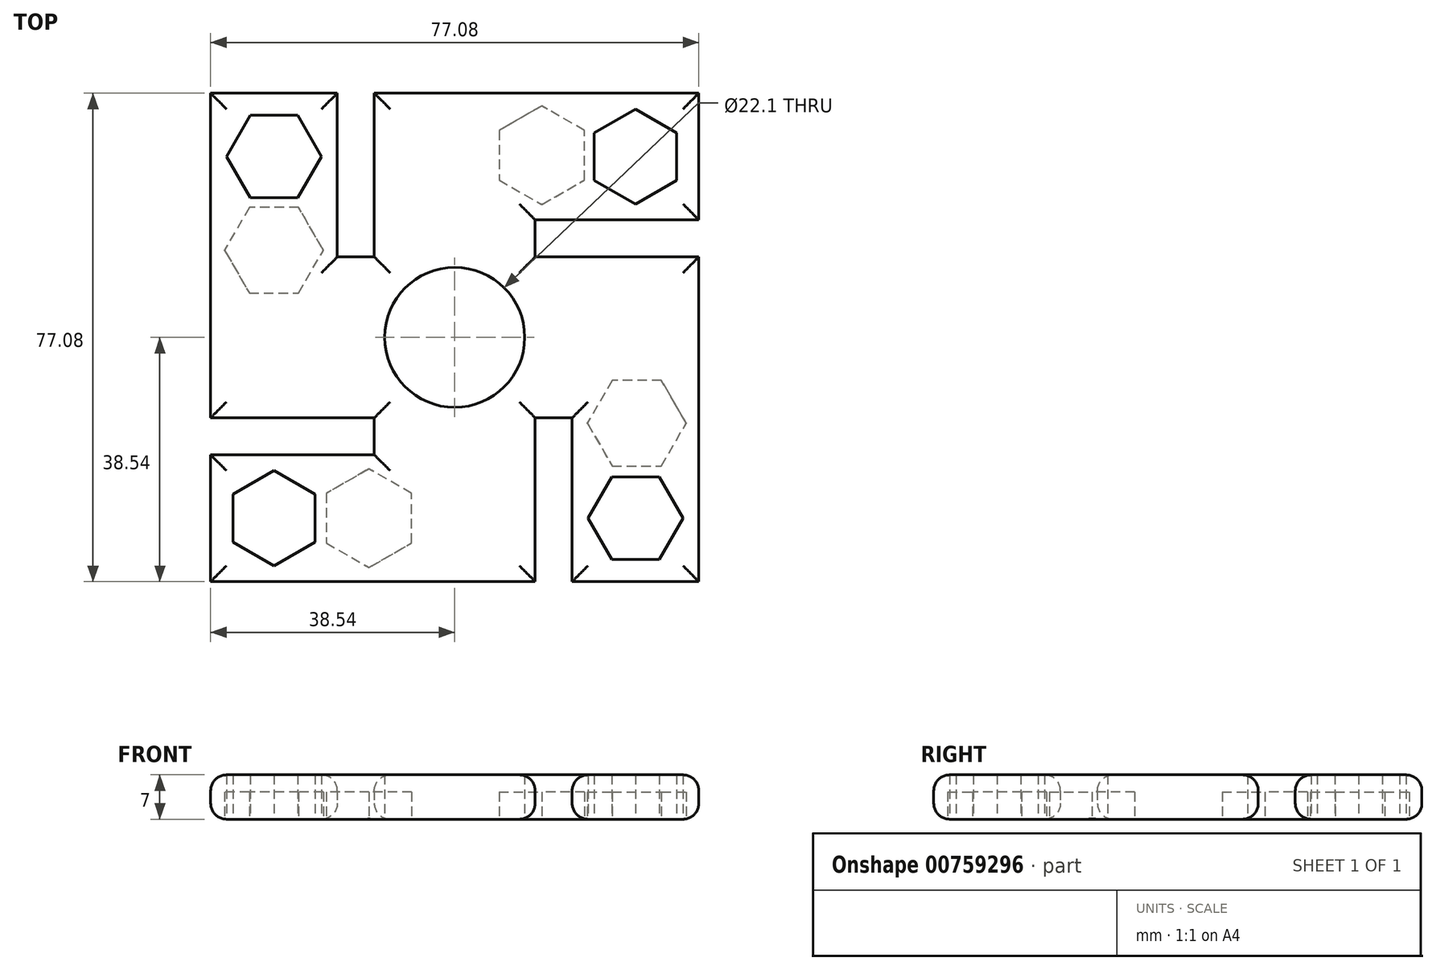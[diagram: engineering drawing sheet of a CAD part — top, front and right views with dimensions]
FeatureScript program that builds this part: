
annotation { "Feature Type Name" : "Feature", "Feature Type Description" : "" }
export const myFeature = defineFeature(function(context is Context, id is Id, definition is map)
    precondition{}
    {
        {
            var Q0;
            Q0=qCreatedBy(makeId("Top.planeOp"),FACE);
            var sketch = newSketch(context, id + "F0", { "sketchPlane" : qUnion([Q0])});
            skCircle(sketch, "E0", {"center": v(0, 0) * mm, "radius": 11.05 * mm});
            skCircle(sketch, "E1", {"center": v(0, 0) * mm, "radius": 12.7 * mm});
            skLineSegment(sketch, "E2.bottom", {"start": v(12.7, 12.7) * mm, "end": v(-12.7, 12.7) * mm});
            skLineSegment(sketch, "E2.top", {"start": v(12.7, -12.7) * mm, "end": v(-12.7, -12.7) * mm});
            skLineSegment(sketch, "E2.left", {"start": v(12.7, 12.7) * mm, "end": v(12.7, -12.7) * mm});
            skLineSegment(sketch, "E2.right", {"start": v(-12.7, 12.7) * mm, "end": v(-12.7, -12.7) * mm});
            skLineSegment(sketch, "E3.bottom", {"start": v(-12.7, 12.7) * mm, "end": v(12.7, 12.7) * mm});
            skLineSegment(sketch, "E3.top", {"start": v(-12.7, 38.54) * mm, "end": v(12.7, 38.54) * mm});
            skLineSegment(sketch, "E3.left", {"start": v(-12.7, 12.7) * mm, "end": v(-12.7, 38.54) * mm});
            skLineSegment(sketch, "E3.right", {"start": v(12.7, 12.7) * mm, "end": v(12.7, 38.54) * mm});
            skLineSegment(sketch, "E4.bottom", {"start": v(12.7, 38.54) * mm, "end": v(38.54, 38.54) * mm});
            skLineSegment(sketch, "E4.top", {"start": v(12.7, 18.54) * mm, "end": v(38.54, 18.54) * mm});
            skLineSegment(sketch, "E4.left", {"start": v(12.7, 38.54) * mm, "end": v(12.7, 18.54) * mm});
            skLineSegment(sketch, "E4.right", {"start": v(38.54, 38.54) * mm, "end": v(38.54, 18.54) * mm});
            skCircle(sketch, "E5.cCircle", {"center": v(28.54, 28.54) * mm, "radius": 6.5 * mm, "construction": true});
            skLineSegment(sketch, "E5.0", {"start": v(35.04, 32.3) * mm, "end": v(35.04, 24.79) * mm});
            skLineSegment(sketch, "E5.1", {"start": v(35.04, 24.79) * mm, "end": v(28.54, 21.03) * mm});
            skLineSegment(sketch, "E5.2", {"start": v(28.54, 21.03) * mm, "end": v(22.04, 24.79) * mm});
            skLineSegment(sketch, "E5.3", {"start": v(22.04, 24.79) * mm, "end": v(22.04, 32.3) * mm});
            skLineSegment(sketch, "E5.4", {"start": v(22.04, 32.3) * mm, "end": v(28.54, 36.05) * mm});
            skLineSegment(sketch, "E5.5", {"start": v(28.54, 36.05) * mm, "end": v(35.04, 32.3) * mm});
            skPoint(sketch, "E5.0.midPoint", {"position": v(35.04, 28.54) * mm});
            skPoint(sketch, "E6.1.0", {"position": v(-28.54, 35.04) * mm});
            skLineSegment(sketch, "E6.1.1", {"start": v(-18.54, 12.7) * mm, "end": v(-18.54, 38.54) * mm});
            skLineSegment(sketch, "E6.1.2", {"start": v(-12.7, -12.7) * mm, "end": v(-38.54, -12.7) * mm});
            skLineSegment(sketch, "E6.1.3", {"start": v(-38.54, 12.7) * mm, "end": v(-38.54, 38.54) * mm});
            skLineSegment(sketch, "E6.1.4", {"start": v(-38.54, -12.7) * mm, "end": v(-38.54, 12.7) * mm});
            skCircle(sketch, "E6.1.5", {"center": v(-28.54, 28.54) * mm, "radius": 6.5 * mm, "construction": true});
            skLineSegment(sketch, "E6.1.6", {"start": v(-12.7, 12.7) * mm, "end": v(-38.54, 12.7) * mm});
            skLineSegment(sketch, "E6.1.7", {"start": v(-12.7, -12.7) * mm, "end": v(-12.7, 12.7) * mm});
            skLineSegment(sketch, "E6.1.8", {"start": v(-38.54, 12.7) * mm, "end": v(-18.54, 12.7) * mm});
            skLineSegment(sketch, "E6.1.9", {"start": v(-38.54, 38.54) * mm, "end": v(-18.54, 38.54) * mm});
            skLineSegment(sketch, "E6.1.10", {"start": v(-32.3, 22.04) * mm, "end": v(-36.05, 28.54) * mm});
            skLineSegment(sketch, "E6.1.11", {"start": v(-21.03, 28.54) * mm, "end": v(-24.79, 22.04) * mm});
            skLineSegment(sketch, "E6.1.12", {"start": v(-24.79, 35.04) * mm, "end": v(-21.03, 28.54) * mm});
            skLineSegment(sketch, "E6.1.13", {"start": v(-36.05, 28.54) * mm, "end": v(-32.3, 35.04) * mm});
            skLineSegment(sketch, "E6.1.15", {"start": v(-24.79, 22.04) * mm, "end": v(-32.3, 22.04) * mm});
            skLineSegment(sketch, "E6.1.16", {"start": v(-32.3, 35.04) * mm, "end": v(-24.79, 35.04) * mm});
            skPoint(sketch, "E6.2.0", {"position": v(-35.04, -28.54) * mm});
            skLineSegment(sketch, "E6.2.1", {"start": v(-12.7, -18.54) * mm, "end": v(-38.54, -18.54) * mm});
            skLineSegment(sketch, "E6.2.2", {"start": v(12.7, -12.7) * mm, "end": v(12.7, -38.54) * mm});
            skLineSegment(sketch, "E6.2.3", {"start": v(-12.7, -38.54) * mm, "end": v(-38.54, -38.54) * mm});
            skLineSegment(sketch, "E6.2.4", {"start": v(12.7, -38.54) * mm, "end": v(-12.7, -38.54) * mm});
            skCircle(sketch, "E6.2.5", {"center": v(-28.54, -28.54) * mm, "radius": 6.5 * mm, "construction": true});
            skLineSegment(sketch, "E6.2.6", {"start": v(-12.7, -12.7) * mm, "end": v(-12.7, -38.54) * mm});
            skLineSegment(sketch, "E6.2.8", {"start": v(-12.7, -38.54) * mm, "end": v(-12.7, -18.54) * mm});
            skLineSegment(sketch, "E6.2.9", {"start": v(-38.54, -38.54) * mm, "end": v(-38.54, -18.54) * mm});
            skLineSegment(sketch, "E6.2.10", {"start": v(-22.04, -32.3) * mm, "end": v(-28.54, -36.05) * mm});
            skLineSegment(sketch, "E6.2.11", {"start": v(-28.54, -21.03) * mm, "end": v(-22.04, -24.79) * mm});
            skLineSegment(sketch, "E6.2.12", {"start": v(-35.04, -24.79) * mm, "end": v(-28.54, -21.03) * mm});
            skLineSegment(sketch, "E6.2.13", {"start": v(-28.54, -36.05) * mm, "end": v(-35.04, -32.3) * mm});
            skLineSegment(sketch, "E6.2.14", {"start": v(-12.7, -12.7) * mm, "end": v(12.7, -12.7) * mm});
            skLineSegment(sketch, "E6.2.15", {"start": v(-22.04, -24.79) * mm, "end": v(-22.04, -32.3) * mm});
            skLineSegment(sketch, "E6.2.16", {"start": v(-35.04, -32.3) * mm, "end": v(-35.04, -24.79) * mm});
            skPoint(sketch, "E6.3.0", {"position": v(28.54, -35.04) * mm});
            skLineSegment(sketch, "E6.3.1", {"start": v(18.54, -12.7) * mm, "end": v(18.54, -38.54) * mm});
            skLineSegment(sketch, "E6.3.2", {"start": v(12.7, 12.7) * mm, "end": v(38.54, 12.7) * mm});
            skLineSegment(sketch, "E6.3.3", {"start": v(38.54, -12.7) * mm, "end": v(38.54, -38.54) * mm});
            skLineSegment(sketch, "E6.3.4", {"start": v(38.54, 12.7) * mm, "end": v(38.54, -12.7) * mm});
            skCircle(sketch, "E6.3.5", {"center": v(28.54, -28.54) * mm, "radius": 6.5 * mm, "construction": true});
            skLineSegment(sketch, "E6.3.6", {"start": v(12.7, -12.7) * mm, "end": v(38.54, -12.7) * mm});
            skLineSegment(sketch, "E6.3.8", {"start": v(38.54, -12.7) * mm, "end": v(18.54, -12.7) * mm});
            skLineSegment(sketch, "E6.3.9", {"start": v(38.54, -38.54) * mm, "end": v(18.54, -38.54) * mm});
            skLineSegment(sketch, "E6.3.10", {"start": v(32.3, -22.04) * mm, "end": v(36.05, -28.54) * mm});
            skLineSegment(sketch, "E6.3.11", {"start": v(21.03, -28.54) * mm, "end": v(24.79, -22.04) * mm});
            skLineSegment(sketch, "E6.3.12", {"start": v(24.79, -35.04) * mm, "end": v(21.03, -28.54) * mm});
            skLineSegment(sketch, "E6.3.13", {"start": v(36.05, -28.54) * mm, "end": v(32.3, -35.04) * mm});
            skLineSegment(sketch, "E6.3.14", {"start": v(12.7, -12.7) * mm, "end": v(12.7, 12.7) * mm});
            skLineSegment(sketch, "E6.3.15", {"start": v(24.79, -22.04) * mm, "end": v(32.3, -22.04) * mm});
            skLineSegment(sketch, "E6.3.16", {"start": v(32.3, -35.04) * mm, "end": v(24.79, -35.04) * mm});
            skSolve(sketch);
        }
        {
            var Q0;
            Q0=makeQuery(id+"F0.imprint","IMPRINT",FACE,{"disambiguationData":[TD([[makeQuery(id+"F0.imprint","IMPRINT",EDGE,{"derivedFrom":sQuery(id+"F0.wireOp",EDGE,"E6.1.1")}),1.0]])]});
            var Q1;
            {var subQ1=sQuery(id+"F0.wireOp",EDGE,"E6.1.2");Q1=makeQuery(id+"F0.imprint","IMPRINT",FACE,{"disambiguationData":[TD([[makeQuery(id+"F0.imprint","IMPRINT",EDGE,{"derivedFrom":subQ1}),-1.0]])]});}
            var Q2;
            {var subQ0=sQuery(id+"F0.wireOp",EDGE,"E3.bottom");var subQ1=sQuery(id+"F0.wireOp",EDGE,"E1");var subQ2=makeQuery(id+"F0.imprint","INTERSECT",VERTEX,{"derivedFrom":[subQ1,subQ0]});Q2=makeQuery(id+"F0.imprint","IMPRINT",FACE,{"disambiguationData":[TD([[makeQuery(id+"F0.imprint","IMPRINT",EDGE,{"disambiguationData":[TD([[subQ2,-1.0]])],"derivedFrom":subQ1}),-1.0]])]});}
            var Q3;
            {var subQ0=sQuery(id+"F0.wireOp",EDGE,"E2.right");var subQ1=sQuery(id+"F0.wireOp",EDGE,"E1");var subQ2=makeQuery(id+"F0.imprint","INTERSECT",VERTEX,{"derivedFrom":[subQ1,subQ0]});Q3=makeQuery(id+"F0.imprint","IMPRINT",FACE,{"disambiguationData":[TD([[makeQuery(id+"F0.imprint","IMPRINT",EDGE,{"disambiguationData":[TD([[subQ2,-1.0]])],"derivedFrom":subQ1}),-1.0]])]});}
            var Q4;
            {var subQ0=sQuery(id+"F0.wireOp",EDGE,"E6.3.14");var subQ1=sQuery(id+"F0.wireOp",EDGE,"E1");var subQ2=makeQuery(id+"F0.imprint","INTERSECT",VERTEX,{"derivedFrom":[subQ1,subQ0]});Q4=makeQuery(id+"F0.imprint","IMPRINT",FACE,{"disambiguationData":[TD([[makeQuery(id+"F0.imprint","IMPRINT",EDGE,{"disambiguationData":[TD([[subQ2,1.0]])],"derivedFrom":subQ1}),-1.0]])]});}
            var Q5;
            {var subQ0=sQuery(id+"F0.wireOp",EDGE,"E3.bottom");var subQ1=sQuery(id+"F0.wireOp",EDGE,"E1");var subQ2=makeQuery(id+"F0.imprint","INTERSECT",VERTEX,{"derivedFrom":[subQ1,subQ0]});Q5=makeQuery(id+"F0.imprint","IMPRINT",FACE,{"disambiguationData":[TD([[makeQuery(id+"F0.imprint","IMPRINT",EDGE,{"disambiguationData":[TD([[subQ2,1.0]])],"derivedFrom":subQ1}),-1.0]])]});}
            var Q6;
            Q6=makeQuery(id+"F0.imprint","IMPRINT",FACE,{"disambiguationData":[TD([[makeQuery(id+"F0.imprint","IMPRINT",EDGE,{"derivedFrom":sQuery(id+"F0.wireOp",EDGE,"E4.bottom")}),-1.0]])]});
            var Q7;
            Q7=makeQuery(id+"F0.imprint","IMPRINT",FACE,{"disambiguationData":[TD([[makeQuery(id+"F0.imprint","IMPRINT",EDGE,{"derivedFrom":sQuery(id+"F0.wireOp",EDGE,"E6.3.1")}),1.0]])]});
            var Q8;
            {var subQ1=sQuery(id+"F0.wireOp",EDGE,"E6.3.2");Q8=makeQuery(id+"F0.imprint","IMPRINT",FACE,{"disambiguationData":[TD([[makeQuery(id+"F0.imprint","IMPRINT",EDGE,{"derivedFrom":subQ1}),-1.0]])]});}
            var Q9;
            {var subQ1=sQuery(id+"F0.wireOp",EDGE,"E6.2.2");Q9=makeQuery(id+"F0.imprint","IMPRINT",FACE,{"disambiguationData":[TD([[makeQuery(id+"F0.imprint","IMPRINT",EDGE,{"derivedFrom":subQ1}),-1.0]])]});}
            var Q10;
            Q10=makeQuery(id+"F0.imprint","IMPRINT",FACE,{"disambiguationData":[TD([[makeQuery(id+"F0.imprint","IMPRINT",EDGE,{"derivedFrom":sQuery(id+"F0.wireOp",EDGE,"E6.2.1")}),1.0]])]});
            var Q11;
            Q11=makeQuery(id+"F0.imprint","IMPRINT",FACE,{"disambiguationData":[TD([[makeQuery(id+"F0.imprint","IMPRINT",EDGE,{"derivedFrom":sQuery(id+"F0.wireOp",EDGE,"E0")}),-1.0]])]});
            var Q12;
            Q12=makeQuery(id+"F0.imprint","IMPRINT",FACE,{"disambiguationData":[TD([[makeQuery(id+"F0.imprint","IMPRINT",EDGE,{"derivedFrom":sQuery(id+"F0.wireOp",EDGE,"E3.top")}),-1.0]])]});
            extrude(context, id + "F1", {"entities" : qUnion([Q0, Q1, Q2, Q3, Q4, Q5, Q6, Q7, Q8, Q9, Q10, Q11, Q12]), "depth" : 7 * mm, "offsetDistance" : 25 * mm});
        }
        {
            var Q0;
            Q0=makeQuery(id+"F1.opExtrude","CAP_FACE",FACE,{"disambiguationData":[OSD([sQuery(id+"F0.wireOp",EDGE,"E0"),sQuery(id+"F0.wireOp",EDGE,"E3.top"),sQuery(id+"F0.wireOp",EDGE,"E3.left"),sQuery(id+"F0.wireOp",EDGE,"E3.right"),sQuery(id+"F0.wireOp",EDGE,"E4.bottom"),sQuery(id+"F0.wireOp",EDGE,"E4.top"),sQuery(id+"F0.wireOp",EDGE,"E4.right"),sQuery(id+"F0.wireOp",EDGE,"E5.0"),sQuery(id+"F0.wireOp",EDGE,"E5.1"),sQuery(id+"F0.wireOp",EDGE,"E5.2"),sQuery(id+"F0.wireOp",EDGE,"E5.3"),sQuery(id+"F0.wireOp",EDGE,"E5.4"),sQuery(id+"F0.wireOp",EDGE,"E5.5"),sQuery(id+"F0.wireOp",EDGE,"E6.1.1"),sQuery(id+"F0.wireOp",EDGE,"E6.1.2"),sQuery(id+"F0.wireOp",EDGE,"E6.1.3"),sQuery(id+"F0.wireOp",EDGE,"E6.1.4"),sQuery(id+"F0.wireOp",EDGE,"E6.1.6"),sQuery(id+"F0.wireOp",EDGE,"E6.1.9"),sQuery(id+"F0.wireOp",EDGE,"E6.1.10"),sQuery(id+"F0.wireOp",EDGE,"E6.1.11"),sQuery(id+"F0.wireOp",EDGE,"E6.1.12"),sQuery(id+"F0.wireOp",EDGE,"E6.1.13"),sQuery(id+"F0.wireOp",EDGE,"E6.1.15"),sQuery(id+"F0.wireOp",EDGE,"E6.1.16"),sQuery(id+"F0.wireOp",EDGE,"E6.2.1"),sQuery(id+"F0.wireOp",EDGE,"E6.2.2"),sQuery(id+"F0.wireOp",EDGE,"E6.2.3"),sQuery(id+"F0.wireOp",EDGE,"E6.2.4"),sQuery(id+"F0.wireOp",EDGE,"E6.2.6"),sQuery(id+"F0.wireOp",EDGE,"E6.2.9"),sQuery(id+"F0.wireOp",EDGE,"E6.2.10"),sQuery(id+"F0.wireOp",EDGE,"E6.2.11"),sQuery(id+"F0.wireOp",EDGE,"E6.2.12"),sQuery(id+"F0.wireOp",EDGE,"E6.2.13"),sQuery(id+"F0.wireOp",EDGE,"E6.2.15"),sQuery(id+"F0.wireOp",EDGE,"E6.2.16"),sQuery(id+"F0.wireOp",EDGE,"E6.3.1"),sQuery(id+"F0.wireOp",EDGE,"E6.3.2"),sQuery(id+"F0.wireOp",EDGE,"E6.3.3"),sQuery(id+"F0.wireOp",EDGE,"E6.3.4"),sQuery(id+"F0.wireOp",EDGE,"E6.3.6"),sQuery(id+"F0.wireOp",EDGE,"E6.3.9"),sQuery(id+"F0.wireOp",EDGE,"E6.3.10"),sQuery(id+"F0.wireOp",EDGE,"E6.3.11"),sQuery(id+"F0.wireOp",EDGE,"E6.3.12"),sQuery(id+"F0.wireOp",EDGE,"E6.3.13"),sQuery(id+"F0.wireOp",EDGE,"E6.3.15"),sQuery(id+"F0.wireOp",EDGE,"E6.3.16")])],"isStart":true});
            var sketch = newSketch(context, id + "F2", { "sketchPlane" : qUnion([Q0])});
            skCircle(sketch, "E7.cCircle", {"center": v(-13.54, 28.54) * mm, "radius": 6.75 * mm, "construction": true});
            skLineSegment(sketch, "E7.0", {"start": v(-20.3, 24.64) * mm, "end": v(-20.3, 32.44) * mm});
            skLineSegment(sketch, "E7.1", {"start": v(-20.3, 32.44) * mm, "end": v(-13.54, 36.33) * mm});
            skLineSegment(sketch, "E7.2", {"start": v(-13.54, 36.33) * mm, "end": v(-6.79, 32.44) * mm});
            skLineSegment(sketch, "E7.3", {"start": v(-6.8, 32.44) * mm, "end": v(-6.8, 24.64) * mm});
            skLineSegment(sketch, "E7.4", {"start": v(-6.8, 24.64) * mm, "end": v(-13.54, 20.75) * mm});
            skLineSegment(sketch, "E7.5", {"start": v(-13.54, 20.75) * mm, "end": v(-20.29, 24.64) * mm});
            skPoint(sketch, "E7.0.midPoint", {"position": v(-20.3, 28.54) * mm});
            skLineSegment(sketch, "E8.1.0", {"start": v(-32.44, -20.5) * mm, "end": v(-36.33, -13.75) * mm});
            skLineSegment(sketch, "E8.1.1", {"start": v(-36.33, -13.75) * mm, "end": v(-32.44, -7) * mm});
            skLineSegment(sketch, "E8.1.2", {"start": v(-32.44, -7) * mm, "end": v(-24.64, -7) * mm});
            skLineSegment(sketch, "E8.1.3", {"start": v(-24.64, -20.5) * mm, "end": v(-32.44, -20.5) * mm});
            skCircle(sketch, "E8.1.4", {"center": v(-28.54, -13.75) * mm, "radius": 6.75 * mm, "construction": true});
            skPoint(sketch, "E8.1.5", {"position": v(-28.54, -20.5) * mm});
            skLineSegment(sketch, "E8.1.6", {"start": v(-24.64, -7) * mm, "end": v(-20.75, -13.75) * mm});
            skLineSegment(sketch, "E8.1.7", {"start": v(-20.75, -13.75) * mm, "end": v(-24.64, -20.5) * mm});
            skLineSegment(sketch, "E8.2.0", {"start": v(20.5, -32.65) * mm, "end": v(13.75, -36.54) * mm});
            skLineSegment(sketch, "E8.2.1", {"start": v(13.75, -36.54) * mm, "end": v(7, -32.65) * mm});
            skLineSegment(sketch, "E8.2.2", {"start": v(7, -32.65) * mm, "end": v(7, -24.85) * mm});
            skLineSegment(sketch, "E8.2.3", {"start": v(20.5, -24.85) * mm, "end": v(20.5, -32.65) * mm});
            skCircle(sketch, "E8.2.4", {"center": v(13.75, -28.75) * mm, "radius": 6.75 * mm, "construction": true});
            skPoint(sketch, "E8.2.5", {"position": v(20.5, -28.75) * mm});
            skLineSegment(sketch, "E8.2.6", {"start": v(7, -24.85) * mm, "end": v(13.75, -20.96) * mm});
            skLineSegment(sketch, "E8.2.7", {"start": v(13.75, -20.96) * mm, "end": v(20.5, -24.85) * mm});
            skLineSegment(sketch, "E8.3.0", {"start": v(32.65, 20.3) * mm, "end": v(36.54, 13.54) * mm});
            skLineSegment(sketch, "E8.3.1", {"start": v(36.54, 13.54) * mm, "end": v(32.65, 6.8) * mm});
            skLineSegment(sketch, "E8.3.2", {"start": v(32.65, 6.8) * mm, "end": v(24.85, 6.8) * mm});
            skLineSegment(sketch, "E8.3.3", {"start": v(24.85, 20.29) * mm, "end": v(32.65, 20.29) * mm});
            skCircle(sketch, "E8.3.4", {"center": v(28.75, 13.54) * mm, "radius": 6.75 * mm, "construction": true});
            skPoint(sketch, "E8.3.5", {"position": v(28.75, 20.3) * mm});
            skLineSegment(sketch, "E8.3.6", {"start": v(24.85, 6.79) * mm, "end": v(20.96, 13.54) * mm});
            skLineSegment(sketch, "E8.3.7", {"start": v(20.96, 13.54) * mm, "end": v(24.85, 20.29) * mm});
            skPoint(sketch, "E8.center", {"position": v(0.1, -0.1) * mm});
            skSolve(sketch);
        }
        {
            var Q0;
            Q0=makeQuery(id+"F2.imprint","IMPRINT",FACE,{"disambiguationData":[TD([[makeQuery(id+"F2.imprint","IMPRINT",EDGE,{"derivedFrom":sQuery(id+"F2.wireOp",EDGE,"E8.1.0")}),-1.0]])]});
            var Q1;
            Q1=makeQuery(id+"F2.imprint","IMPRINT",FACE,{"disambiguationData":[TD([[makeQuery(id+"F2.imprint","IMPRINT",EDGE,{"derivedFrom":sQuery(id+"F2.wireOp",EDGE,"E8.2.0")}),-1.0]])]});
            var Q2;
            Q2=makeQuery(id+"F2.imprint","IMPRINT",FACE,{"disambiguationData":[TD([[makeQuery(id+"F2.imprint","IMPRINT",EDGE,{"derivedFrom":sQuery(id+"F2.wireOp",EDGE,"E8.3.0")}),-1.0]])]});
            var Q3;
            Q3=makeQuery(id+"F2.imprint","IMPRINT",FACE,{"disambiguationData":[TD([[makeQuery(id+"F2.imprint","IMPRINT",EDGE,{"derivedFrom":sQuery(id+"F2.wireOp",EDGE,"E7.0")}),-1.0]])]});
            extrude(context, id + "F3", {"entities" : qUnion([Q0, Q1, Q2, Q3]), "operationType" : NewBodyOperationType.REMOVE, "oppositeDirection" : true, "depth" : 4.28 * mm, "offsetDistance" : 25 * mm});
        }
        {
            var Q0;
            Q0=makeQuery(id+"F1.opExtrude","CAP_EDGE",EDGE,{"disambiguationData":[OSD([sQuery(id+"F0.wireOp",EDGE,"E6.1.3"),sQuery(id+"F0.wireOp",EDGE,"E6.1.4")])],"isStart":false});
            var Q1;
            Q1=makeQuery(id+"F1.opExtrude","CAP_EDGE",EDGE,{"disambiguationData":[OSD([sQuery(id+"F0.wireOp",EDGE,"E6.1.9")])],"isStart":false});
            var Q2;
            Q2=makeQuery(id+"F1.opExtrude","CAP_EDGE",EDGE,{"disambiguationData":[OSD([sQuery(id+"F0.wireOp",EDGE,"E6.1.1")])],"isStart":false});
            var Q3;
            Q3=makeQuery(id+"F1.opExtrude","CAP_EDGE",EDGE,{"disambiguationData":[OSD([sQuery(id+"F0.wireOp",EDGE,"E6.1.6")])],"isStart":false});
            var Q4;
            Q4=makeQuery(id+"F1.opExtrude","CAP_EDGE",EDGE,{"disambiguationData":[OSD([sQuery(id+"F0.wireOp",EDGE,"E3.left")])],"isStart":false});
            var Q5;
            Q5=makeQuery(id+"F1.opExtrude","CAP_EDGE",EDGE,{"disambiguationData":[OSD([sQuery(id+"F0.wireOp",EDGE,"E3.top"),sQuery(id+"F0.wireOp",EDGE,"E4.bottom")])],"isStart":false});
            var Q6;
            Q6=makeQuery(id+"F1.opExtrude","CAP_EDGE",EDGE,{"disambiguationData":[OSD([sQuery(id+"F0.wireOp",EDGE,"E4.right")])],"isStart":false});
            var Q7;
            Q7=makeQuery(id+"F1.opExtrude","CAP_EDGE",EDGE,{"disambiguationData":[OSD([sQuery(id+"F0.wireOp",EDGE,"E4.top")])],"isStart":false});
            var Q8;
            Q8=makeQuery(id+"F1.opExtrude","CAP_EDGE",EDGE,{"disambiguationData":[OSD([sQuery(id+"F0.wireOp",EDGE,"E3.right")])],"isStart":false});
            var Q9;
            Q9=makeQuery(id+"F1.opExtrude","CAP_EDGE",EDGE,{"disambiguationData":[OSD([sQuery(id+"F0.wireOp",EDGE,"E6.3.2")])],"isStart":false});
            var Q10;
            Q10=makeQuery(id+"F1.opExtrude","CAP_EDGE",EDGE,{"disambiguationData":[OSD([sQuery(id+"F0.wireOp",EDGE,"E6.3.3"),sQuery(id+"F0.wireOp",EDGE,"E6.3.4")])],"isStart":false});
            var Q11;
            Q11=makeQuery(id+"F1.opExtrude","CAP_EDGE",EDGE,{"disambiguationData":[OSD([sQuery(id+"F0.wireOp",EDGE,"E6.3.9")])],"isStart":false});
            var Q12;
            Q12=makeQuery(id+"F1.opExtrude","CAP_EDGE",EDGE,{"disambiguationData":[OSD([sQuery(id+"F0.wireOp",EDGE,"E6.3.1")])],"isStart":false});
            var Q13;
            Q13=makeQuery(id+"F1.opExtrude","CAP_EDGE",EDGE,{"disambiguationData":[OSD([sQuery(id+"F0.wireOp",EDGE,"E6.3.6")])],"isStart":false});
            var Q14;
            Q14=makeQuery(id+"F1.opExtrude","CAP_EDGE",EDGE,{"disambiguationData":[OSD([sQuery(id+"F0.wireOp",EDGE,"E6.2.2")])],"isStart":false});
            var Q15;
            Q15=makeQuery(id+"F1.opExtrude","CAP_EDGE",EDGE,{"disambiguationData":[OSD([sQuery(id+"F0.wireOp",EDGE,"E6.2.3"),sQuery(id+"F0.wireOp",EDGE,"E6.2.4")])],"isStart":false});
            var Q16;
            Q16=makeQuery(id+"F1.opExtrude","CAP_EDGE",EDGE,{"disambiguationData":[OSD([sQuery(id+"F0.wireOp",EDGE,"E6.1.2")])],"isStart":false});
            var Q17;
            Q17=makeQuery(id+"F1.opExtrude","CAP_EDGE",EDGE,{"disambiguationData":[OSD([sQuery(id+"F0.wireOp",EDGE,"E6.2.6")])],"isStart":false});
            var Q18;
            Q18=makeQuery(id+"F1.opExtrude","CAP_EDGE",EDGE,{"disambiguationData":[OSD([sQuery(id+"F0.wireOp",EDGE,"E6.2.1")])],"isStart":false});
            var Q19;
            Q19=makeQuery(id+"F1.opExtrude","CAP_EDGE",EDGE,{"disambiguationData":[OSD([sQuery(id+"F0.wireOp",EDGE,"E6.2.9")])],"isStart":false});
            fillet(context, id + "F4", {"entities" : qUnion([Q0, Q1, Q2, Q3, Q4, Q5, Q6, Q7, Q8, Q9, Q10, Q11, Q12, Q13, Q14, Q15, Q16, Q17, Q18, Q19]), "radius" : 2.5 * mm, "tangentPropagation" : true, "allowEdgeOverflow" : false});
        }
        {
            var Q0;
            Q0=makeQuery(id+"F1.opExtrude","CAP_EDGE",EDGE,{"disambiguationData":[OSD([sQuery(id+"F0.wireOp",EDGE,"E6.2.3"),sQuery(id+"F0.wireOp",EDGE,"E6.2.4")])],"isStart":true});
            var Q1;
            Q1=makeQuery(id+"F1.opExtrude","CAP_EDGE",EDGE,{"disambiguationData":[OSD([sQuery(id+"F0.wireOp",EDGE,"E6.2.9")])],"isStart":true});
            var Q2;
            Q2=makeQuery(id+"F1.opExtrude","CAP_EDGE",EDGE,{"disambiguationData":[OSD([sQuery(id+"F0.wireOp",EDGE,"E6.2.1")])],"isStart":true});
            var Q3;
            Q3=makeQuery(id+"F1.opExtrude","CAP_EDGE",EDGE,{"disambiguationData":[OSD([sQuery(id+"F0.wireOp",EDGE,"E6.2.6")])],"isStart":true});
            var Q4;
            Q4=makeQuery(id+"F1.opExtrude","CAP_EDGE",EDGE,{"disambiguationData":[OSD([sQuery(id+"F0.wireOp",EDGE,"E6.2.2")])],"isStart":true});
            var Q5;
            Q5=makeQuery(id+"F1.opExtrude","CAP_EDGE",EDGE,{"disambiguationData":[OSD([sQuery(id+"F0.wireOp",EDGE,"E6.3.6")])],"isStart":true});
            var Q6;
            Q6=makeQuery(id+"F1.opExtrude","CAP_EDGE",EDGE,{"disambiguationData":[OSD([sQuery(id+"F0.wireOp",EDGE,"E6.3.1")])],"isStart":true});
            var Q7;
            Q7=makeQuery(id+"F1.opExtrude","CAP_EDGE",EDGE,{"disambiguationData":[OSD([sQuery(id+"F0.wireOp",EDGE,"E6.3.9")])],"isStart":true});
            var Q8;
            Q8=makeQuery(id+"F1.opExtrude","CAP_EDGE",EDGE,{"disambiguationData":[OSD([sQuery(id+"F0.wireOp",EDGE,"E6.3.3"),sQuery(id+"F0.wireOp",EDGE,"E6.3.4")])],"isStart":true});
            var Q9;
            Q9=makeQuery(id+"F1.opExtrude","CAP_EDGE",EDGE,{"disambiguationData":[OSD([sQuery(id+"F0.wireOp",EDGE,"E6.3.2")])],"isStart":true});
            var Q10;
            Q10=makeQuery(id+"F1.opExtrude","CAP_EDGE",EDGE,{"disambiguationData":[OSD([sQuery(id+"F0.wireOp",EDGE,"E3.right")])],"isStart":true});
            var Q11;
            Q11=makeQuery(id+"F1.opExtrude","CAP_EDGE",EDGE,{"disambiguationData":[OSD([sQuery(id+"F0.wireOp",EDGE,"E4.top")])],"isStart":true});
            var Q12;
            Q12=makeQuery(id+"F1.opExtrude","CAP_EDGE",EDGE,{"disambiguationData":[OSD([sQuery(id+"F0.wireOp",EDGE,"E4.right")])],"isStart":true});
            var Q13;
            Q13=makeQuery(id+"F1.opExtrude","CAP_EDGE",EDGE,{"disambiguationData":[OSD([sQuery(id+"F0.wireOp",EDGE,"E3.top"),sQuery(id+"F0.wireOp",EDGE,"E4.bottom")])],"isStart":true});
            var Q14;
            Q14=makeQuery(id+"F1.opExtrude","CAP_EDGE",EDGE,{"disambiguationData":[OSD([sQuery(id+"F0.wireOp",EDGE,"E3.left")])],"isStart":true});
            var Q15;
            Q15=makeQuery(id+"F1.opExtrude","CAP_EDGE",EDGE,{"disambiguationData":[OSD([sQuery(id+"F0.wireOp",EDGE,"E6.1.6")])],"isStart":true});
            var Q16;
            Q16=makeQuery(id+"F1.opExtrude","CAP_EDGE",EDGE,{"disambiguationData":[OSD([sQuery(id+"F0.wireOp",EDGE,"E6.1.1")])],"isStart":true});
            var Q17;
            Q17=makeQuery(id+"F1.opExtrude","CAP_EDGE",EDGE,{"disambiguationData":[OSD([sQuery(id+"F0.wireOp",EDGE,"E6.1.9")])],"isStart":true});
            var Q18;
            Q18=makeQuery(id+"F1.opExtrude","CAP_EDGE",EDGE,{"disambiguationData":[OSD([sQuery(id+"F0.wireOp",EDGE,"E6.1.3"),sQuery(id+"F0.wireOp",EDGE,"E6.1.4")])],"isStart":true});
            var Q19;
            Q19=makeQuery(id+"F1.opExtrude","CAP_EDGE",EDGE,{"disambiguationData":[OSD([sQuery(id+"F0.wireOp",EDGE,"E6.1.2")])],"isStart":true});
            fillet(context, id + "F5", {"entities" : qUnion([Q0, Q1, Q2, Q3, Q4, Q5, Q6, Q7, Q8, Q9, Q10, Q11, Q12, Q13, Q14, Q15, Q16, Q17, Q18, Q19]), "radius" : 2.5 * mm, "tangentPropagation" : true, "allowEdgeOverflow" : false});
        }
    });
